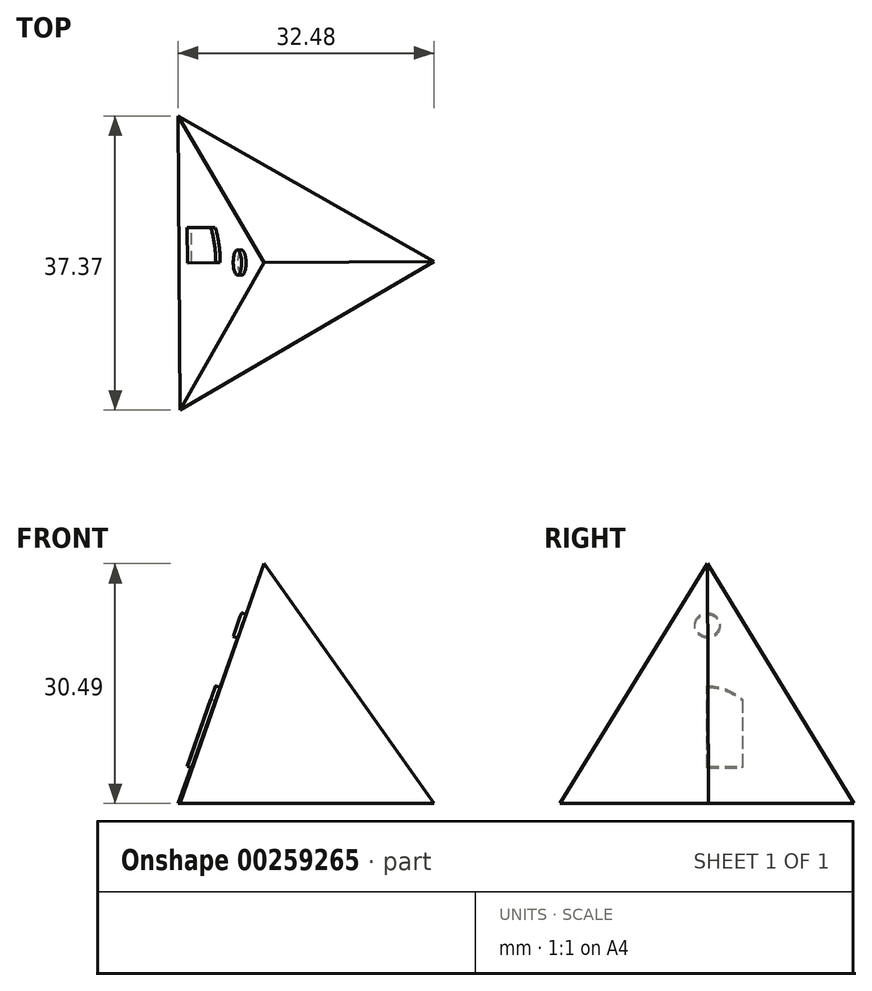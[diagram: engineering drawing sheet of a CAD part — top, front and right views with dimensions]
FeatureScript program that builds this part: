
annotation { "Feature Type Name" : "Feature", "Feature Type Description" : "" }
export const myFeature = defineFeature(function(context is Context, id is Id, definition is map)
    precondition{}
    {
        {
            assignVariable(context, id + "F0", {"name" : "d", "anyValue" : .6});
        }
        {
            var Q0;
            Q0=qCreatedBy(makeId("Top.planeOp"),FACE);
            var sketch = newSketch(context, id + "F1", { "sketchPlane" : qUnion([Q0])});
            skCircle(sketch, "E0.cCircle", {"center": v(0, 0) * mm, "radius": 11 * mm, "construction": true});
            skLineSegment(sketch, "E0.0", {"start": v(-11.12, 18.98) * mm, "end": v(22, 0.14) * mm});
            skLineSegment(sketch, "E0.1", {"start": v(22, 0.14) * mm, "end": v(-10.88, -19.12) * mm});
            skLineSegment(sketch, "E0.2", {"start": v(-10.88, -19.12) * mm, "end": v(-11.12, 18.98) * mm});
            skPoint(sketch, "E0.0.midPoint", {"position": v(5.44, 9.56) * mm});
            skSolve(sketch);
        }
        {
            var Q0;
            Q0=qCreatedBy(makeId("Front.planeOp"),FACE);
            var sketch = newSketch(context, id + "F2", { "sketchPlane" : qUnion([Q0])});
            skPoint(sketch, "E1", {"position": v(0, 0) * mm});
            skPoint(sketch, "E2", {"position": v(0, 31.09) * mm});
            skSolve(sketch);
        }
        {
            var Q0;
            Q0=makeQuery(id+"F1.imprint","IMPRINT",FACE,{"disambiguationData":[TD([[makeQuery(id+"F1.imprint","IMPRINT",EDGE,{"derivedFrom":sQuery(id+"F1.wireOp",EDGE,"E0.0")}),-1.0]])]});
            var Q1;
            Q1=sQuery(id+"F2.wireOp",VERTEX,"E2");
            loft(context, id + "F3", {"sheetProfilesArray" : [{ "sheetProfileEntities" : qUnion([Q0]) }, { "sheetProfileEntities" : qUnion([Q1]) }]});
        }
        {
            var Q0;
            {var subQ0=sQuery(id+"F1.wireOp",EDGE,"E0.2");var subQ1=sQuery(id+"F1.wireOp",EDGE,"E0.1");var subQ2=sQuery(id+"F1.wireOp",EDGE,"E0.0");Q0=makeQuery(id+"F3.opLoft","SWEPT_FACE",FACE,{"disambiguationData":[OSD([subQ2,subQ1,subQ0]),TDD([makeQuery(id+"F1.imprint","INTERSECT",VERTEX,{"derivedFrom":[subQ2,subQ0]}),makeQuery(id+"F1.imprint","INTERSECT",VERTEX,{"derivedFrom":[subQ1,subQ0]}),makeQuery(id+"F1.imprint","IMPRINT",EDGE,{"derivedFrom":subQ0})])]});}
            var sketch = newSketch(context, id + "F4", { "sketchPlane" : qUnion([Q0])});
            skLineSegment(sketch, "E3", {"start": v(0, -3.67) * mm, "end": v(-0.03, 12.2) * mm});
            skLineSegment(sketch, "E4.top", {"start": v(4.47, 1.37) * mm, "end": v(-4.5, 1.37) * mm});
            skLineSegment(sketch, "E4.left", {"start": v(4.47, 10.35) * mm, "end": v(4.47, 1.37) * mm});
            skLineSegment(sketch, "E4.right", {"start": v(-4.5, 10.35) * mm, "end": v(-4.5, 1.37) * mm});
            skPoint(sketch, "E4.middle", {"position": v(-0.02, 5.86) * mm});
            skArc(sketch, "E5", {"start": v(4.47, 10.35) * mm, "mid": v(-0.02, 12.2) * mm, "end": v(-4.5, 10.35) * mm});
            skLineSegment(sketch, "E6.trimOffspring", {"start": v(-0.03, 12.2) * mm, "end": v(-0.06, 29.3) * mm});
            skCircle(sketch, "E7", {"center": v(-0.04, 20.44) * mm, "radius": 1.59 * mm});
            skCircle(sketch, "E8", {"center": v(-1.2, 8.2) * mm, "radius": 0.72 * mm});
            skSolve(sketch);
        }
        {
            var Q0;
            {var subQ1=sQuery(id+"F4.wireOp",EDGE,"E4.left");Q0=makeQuery(id+"F4.imprint","IMPRINT",FACE,{"disambiguationData":[TD([[makeQuery(id+"F4.imprint","IMPRINT",EDGE,{"derivedFrom":subQ1}),-1.0]])]});}
            var Q1;
            {var subQ0=sQuery(id+"F4.wireOp",EDGE,"E7");var subQ1=sQuery(id+"F4.wireOp",EDGE,"E6.trimOffspring");var subQ2=makeQuery(id+"F4.imprint","INTERSECT",VERTEX,{"disambiguationData":[OD(0.0)],"derivedFrom":[subQ1,subQ0]});Q1=makeQuery(id+"F4.imprint","IMPRINT",FACE,{"disambiguationData":[TD([[makeQuery(id+"F4.imprint","IMPRINT",EDGE,{"disambiguationData":[TD([[subQ2,-1.0]])],"derivedFrom":subQ1}),-1.0]])]});}
            var Q2;
            {var subQ0=sQuery(id+"F4.wireOp",EDGE,"E7");var subQ1=sQuery(id+"F4.wireOp",EDGE,"E6.trimOffspring");var subQ2=makeQuery(id+"F4.imprint","INTERSECT",VERTEX,{"disambiguationData":[OD(0.0)],"derivedFrom":[subQ1,subQ0]});Q2=makeQuery(id+"F4.imprint","IMPRINT",FACE,{"disambiguationData":[TD([[makeQuery(id+"F4.imprint","IMPRINT",EDGE,{"disambiguationData":[TD([[subQ2,-1.0]])],"derivedFrom":subQ1}),1.0]])]});}
            extrude(context, id + "F5", {"entities" : qUnion([Q0, Q1, Q2]), "operationType" : NewBodyOperationType.REMOVE, "oppositeDirection" : true, "depth" : (getVariable(context, 'd')) * mm});
        }
    });
